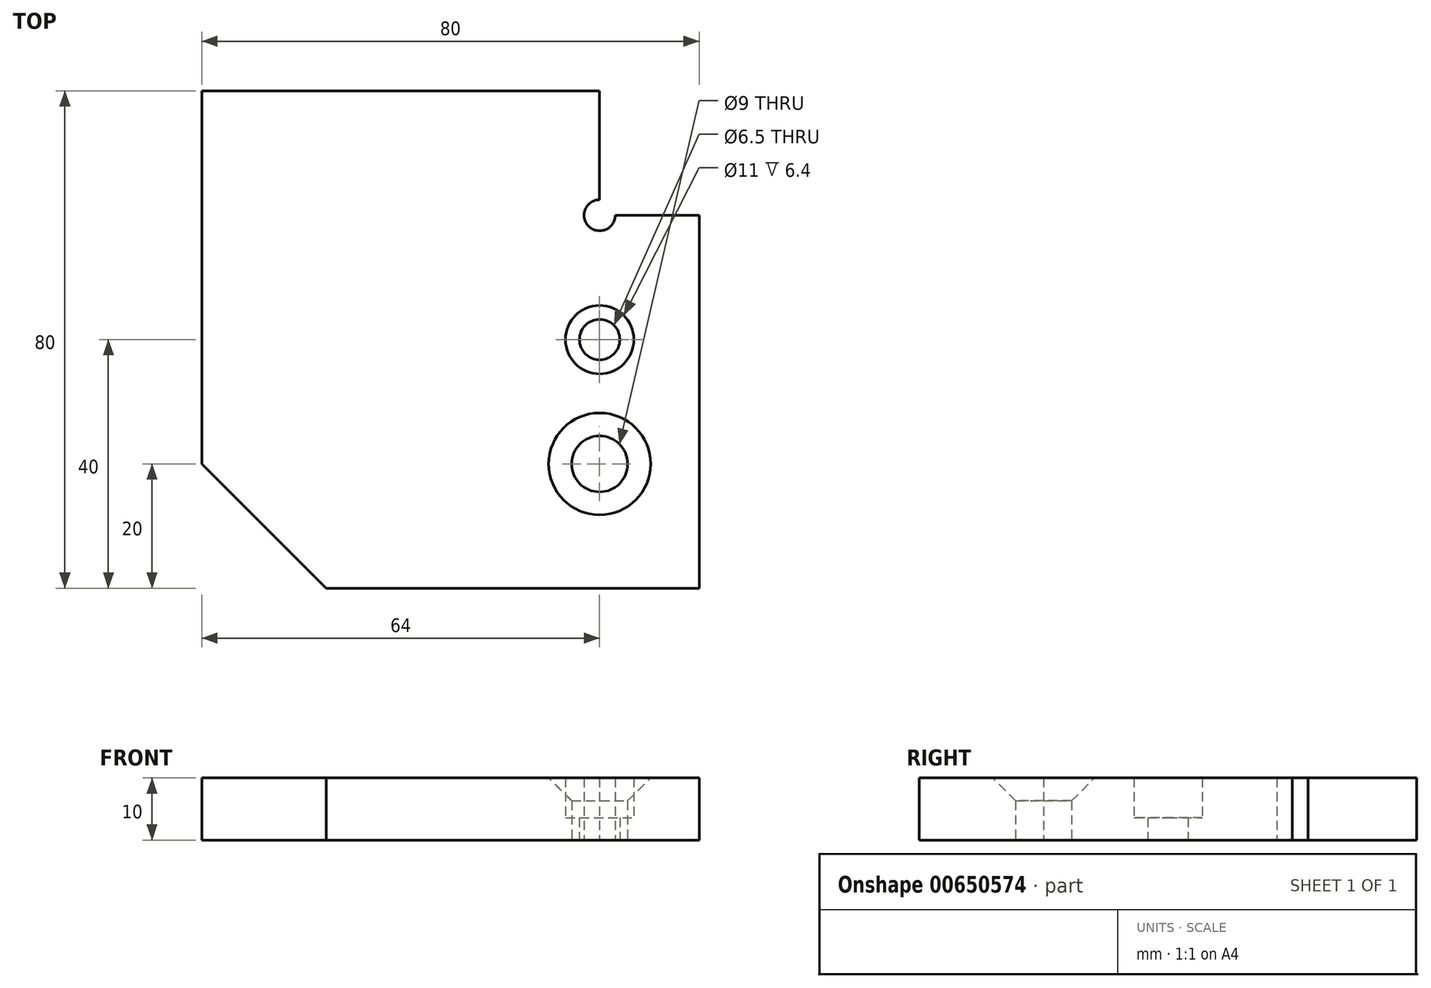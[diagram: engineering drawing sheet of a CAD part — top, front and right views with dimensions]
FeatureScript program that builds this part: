
annotation { "Feature Type Name" : "Feature", "Feature Type Description" : "" }
export const myFeature = defineFeature(function(context is Context, id is Id, definition is map)
    precondition{}
    {
        {
            var Q0;
            Q0=qCreatedBy(makeId("Top.planeOp"),FACE);
            var sketch = newSketch(context, id + "F0", { "sketchPlane" : qUnion([Q0])});
            skLineSegment(sketch, "E0", {"start": v(20, 0) * mm, "end": v(80, 0) * mm});
            skLineSegment(sketch, "E1", {"start": v(80, 0) * mm, "end": v(80, 60) * mm});
            skLineSegment(sketch, "E2", {"start": v(80, 60) * mm, "end": v(66.5, 60) * mm});
            skLineSegment(sketch, "E3", {"start": v(64, 80) * mm, "end": v(64, 62.5) * mm});
            skLineSegment(sketch, "E4", {"start": v(64, 80) * mm, "end": v(0, 80) * mm});
            skLineSegment(sketch, "E5", {"start": v(0, 80) * mm, "end": v(0, 20) * mm});
            skLineSegment(sketch, "E6", {"start": v(0, 20) * mm, "end": v(20, 0) * mm});
            skArc(sketch, "E7", {"start": v(64, 62.5) * mm, "mid": v(62.23, 58.23) * mm, "end": v(66.5, 60) * mm});
            skSolve(sketch);
        }
        {
            var Q0;
            Q0=makeQuery(id+"F0.imprint","IMPRINT",FACE,{"disambiguationData":[TD([[makeQuery(id+"F0.imprint","IMPRINT",EDGE,{"derivedFrom":sQuery(id+"F0.wireOp",EDGE,"E0")}),1.0]])]});
            extrude(context, id + "F1", {"entities" : qUnion([Q0]), "depth" : 10 * mm, "offsetDistance" : 25 * mm});
        }
        {
            var Q0;
            Q0=makeQuery(id+"F1.opExtrude","CAP_FACE",FACE,{"disambiguationData":[OSD([sQuery(id+"F0.wireOp",EDGE,"E0"),sQuery(id+"F0.wireOp",EDGE,"E1"),sQuery(id+"F0.wireOp",EDGE,"E2"),sQuery(id+"F0.wireOp",EDGE,"E3"),sQuery(id+"F0.wireOp",EDGE,"E4"),sQuery(id+"F0.wireOp",EDGE,"E5"),sQuery(id+"F0.wireOp",EDGE,"E6"),sQuery(id+"F0.wireOp",EDGE,"E7")])],"isStart":false});
            var sketch = newSketch(context, id + "F2", { "sketchPlane" : qUnion([Q0])});
            skPoint(sketch, "E8", {"position": v(16, 27) * mm});
            skPoint(sketch, "E9", {"position": v(16, 53) * mm});
            skPoint(sketch, "E10", {"position": v(64, 20) * mm});
            skPoint(sketch, "E11.0.1.0", {"position": v(64, 40) * mm});
            skPoint(sketch, "E11.1.0.0", {"position": v(48, 20) * mm});
            skPoint(sketch, "E11.1.1.0", {"position": v(48, 40) * mm});
            skPoint(sketch, "E11.2.0.0", {"position": v(32, 20) * mm});
            skPoint(sketch, "E11.2.1.0", {"position": v(32, 40) * mm});
            skLineSegment(sketch, "E11.direction1", {"start": v(64, 20) * mm, "end": v(48, 20) * mm, "construction": true});
            skLineSegment(sketch, "E11.direction2", {"start": v(64, 20) * mm, "end": v(64, 40) * mm, "construction": true});
            skSolve(sketch);
        }
        {
            var Q0;
            Q0=sQuery(id+"F2.wireOp",VERTEX,"E10");
            var Q1;
            Q1=makeQuery(id+"F1.opExtrude","SWEPT_BODY",BODY,{"disambiguationData":[OSD([sQuery(id+"F0.wireOp",EDGE,"E0"),sQuery(id+"F0.wireOp",EDGE,"E1"),sQuery(id+"F0.wireOp",EDGE,"E2"),sQuery(id+"F0.wireOp",EDGE,"E3"),sQuery(id+"F0.wireOp",EDGE,"E4"),sQuery(id+"F0.wireOp",EDGE,"E5"),sQuery(id+"F0.wireOp",EDGE,"E6"),sQuery(id+"F0.wireOp",EDGE,"E7")])]});
            hole(context, id + "F3", {"style" : HoleStyle.C_SINK, "endStyle" : HoleEndStyle.THROUGH, "holeDiameter" : 9 * mm, "cSinkDiameter" : 16.4 * mm, "cSinkAngle" : 90 * degree, "majorDiameter" : 5 * mm, "isTappedThrough" : true, "tappedDepth" : 12 * mm, "tapClearance" : 3, "locations" : qUnion([Q0]), "scope" : qUnion([Q1]), "startStyle" : HoleStartStyle.PART});
        }
        {
            var Q0;
            Q0=sQuery(id+"F2.wireOp",VERTEX,"E11.0.1.0");
            var Q1;
            Q1=makeQuery(id+"F1.opExtrude","SWEPT_BODY",BODY,{"disambiguationData":[OSD([sQuery(id+"F0.wireOp",EDGE,"E0"),sQuery(id+"F0.wireOp",EDGE,"E1"),sQuery(id+"F0.wireOp",EDGE,"E2"),sQuery(id+"F0.wireOp",EDGE,"E3"),sQuery(id+"F0.wireOp",EDGE,"E4"),sQuery(id+"F0.wireOp",EDGE,"E5"),sQuery(id+"F0.wireOp",EDGE,"E6"),sQuery(id+"F0.wireOp",EDGE,"E7")])]});
            hole(context, id + "F4", {"style" : HoleStyle.C_BORE, "endStyle" : HoleEndStyle.THROUGH, "holeDiameter" : 6.5 * mm, "cBoreDiameter" : 11 * mm, "cBoreDepth" : 6.4 * mm, "majorDiameter" : 5 * mm, "isTappedThrough" : true, "tappedDepth" : 12 * mm, "tapClearance" : 3, "locations" : qUnion([Q0]), "scope" : qUnion([Q1]), "startStyle" : HoleStartStyle.PART});
        }
    });
